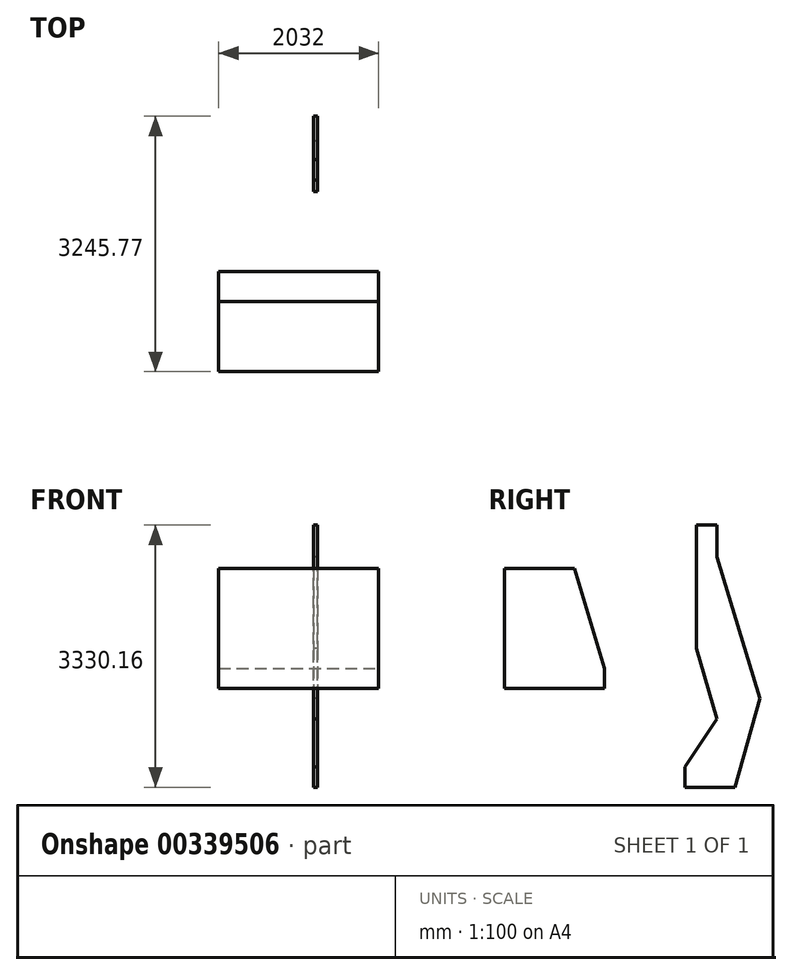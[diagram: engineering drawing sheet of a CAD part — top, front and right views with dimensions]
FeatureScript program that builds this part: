
annotation { "Feature Type Name" : "Feature", "Feature Type Description" : "" }
export const myFeature = defineFeature(function(context is Context, id is Id, definition is map)
    precondition{}
    {
        {
            var Q0;
            Q0=qCreatedBy(makeId("Front.planeOp"),FACE);
            var sketch = newSketch(context, id + "F0", { "sketchPlane" : qUnion([Q0])});
            skLineSegment(sketch, "E0.bottom", {"start": v(-1203.07, 1155.59) * mm, "end": v(828.93, 1155.59) * mm});
            skLineSegment(sketch, "E0.top", {"start": v(-1203.07, -368.41) * mm, "end": v(828.93, -368.41) * mm});
            skLineSegment(sketch, "E0.left", {"start": v(-1203.07, 1155.59) * mm, "end": v(-1203.07, -368.41) * mm});
            skLineSegment(sketch, "E0.right", {"start": v(828.93, 1155.59) * mm, "end": v(828.93, -368.41) * mm});
            skSolve(sketch);
        }
        {
            var Q0;
            Q0=makeQuery(id+"F0.imprint","IMPRINT",FACE,{"disambiguationData":[TD([[makeQuery(id+"F0.imprint","IMPRINT",EDGE,{"derivedFrom":sQuery(id+"F0.wireOp",EDGE,"E0.bottom")}),-1.0]])]});
            extrude(context, id + "F1", {"entities" : qUnion([Q0]), "depth" : 1270 * mm});
        }
        {
            var Q0;
            Q0=makeQuery(id+"F1.opExtrude","CAP_EDGE",EDGE,{"disambiguationData":[OSD([sQuery(id+"F0.wireOp",EDGE,"E0.bottom")])],"isStart":true});
            chamfer(context, id + "F2", {"entities" : qUnion([Q0]), "chamferType" : ChamferType.TWO_OFFSETS, "width1" : 1270 * mm, "oppositeDirection" : false, "width2" : 381 * mm, "tangentPropagation" : true});
        }
        {
            var Q0;
            Q0=qCreatedBy(makeId("Right.planeOp"),FACE);
            var sketch = newSketch(context, id + "F3", { "sketchPlane" : qUnion([Q0])});
            skLineSegment(sketch, "E1", {"start": v(1425.57, 1706.19) * mm, "end": v(1164.95, 1706.19) * mm});
            skLineSegment(sketch, "E2", {"start": v(1164.95, 1706.19) * mm, "end": v(1164.95, 142.46) * mm});
            skLineSegment(sketch, "E3", {"start": v(1657.23, -1623.97) * mm, "end": v(1020.16, -1623.97) * mm});
            skLineSegment(sketch, "E4", {"start": v(1020.16, -1623.97) * mm, "end": v(1020.16, -1363.35) * mm});
            skLineSegment(sketch, "E5", {"start": v(1425.57, 1706.19) * mm, "end": v(1425.57, 1300.78) * mm});
            skLineSegment(sketch, "E6", {"start": v(1657.23, -1623.97) * mm, "end": v(1975.77, -494.61) * mm});
            skLineSegment(sketch, "E7", {"start": v(1975.77, -494.61) * mm, "end": v(1425.57, 1300.78) * mm});
            skLineSegment(sketch, "E8", {"start": v(1164.95, 142.46) * mm, "end": v(1425.57, -755.23) * mm});
            skLineSegment(sketch, "E9", {"start": v(1425.57, -755.23) * mm, "end": v(1020.16, -1363.35) * mm});
            skSolve(sketch);
        }
        {
            var Q0;
            Q0 = qSketchRegion(id + "F3", true);
            extrude(context, id + "F4", {"entities" : qUnion([Q0]), "depth" : 50.8 * mm});
        }
    });
